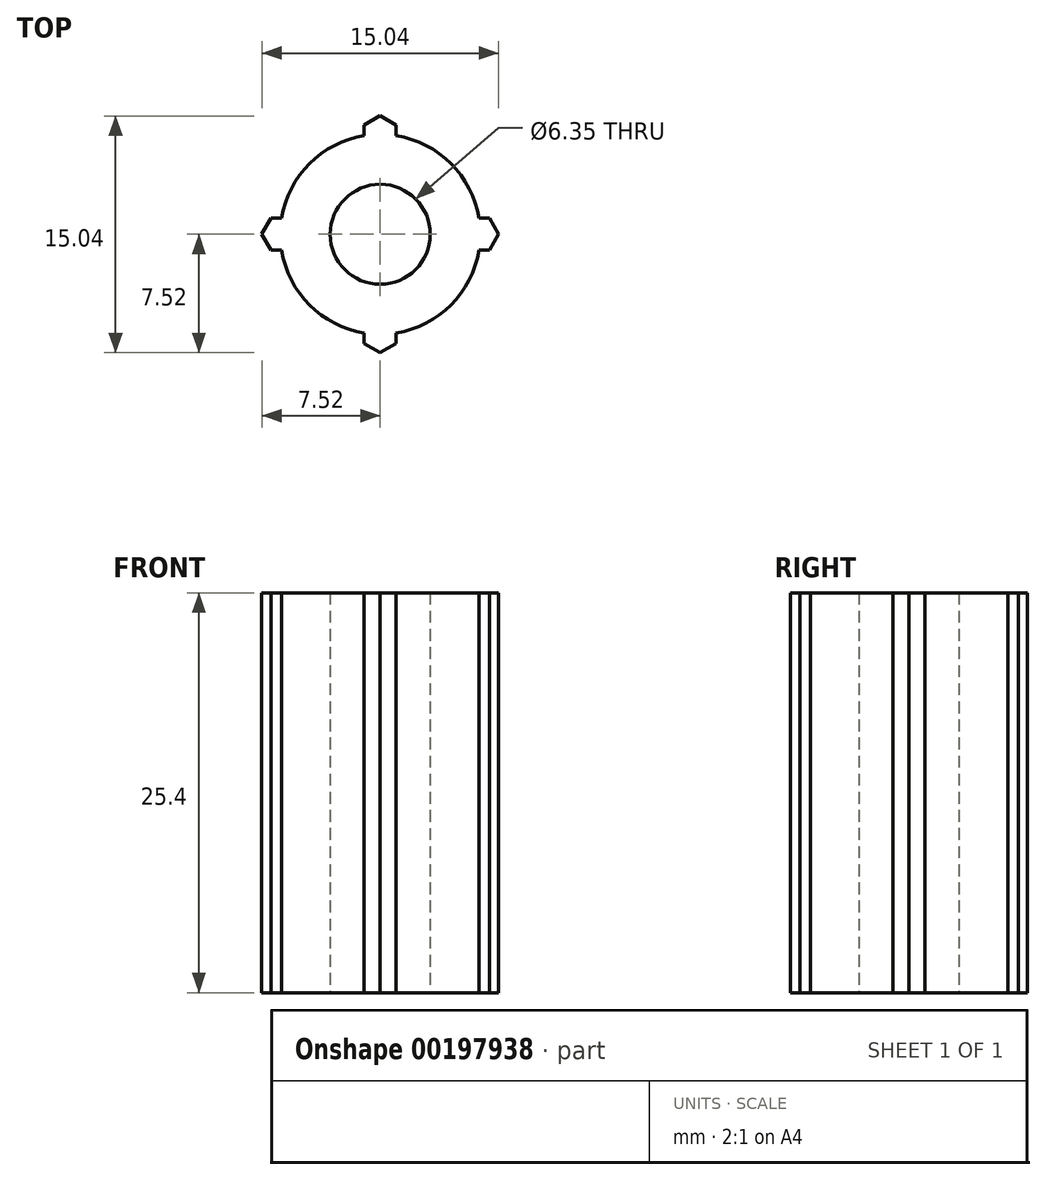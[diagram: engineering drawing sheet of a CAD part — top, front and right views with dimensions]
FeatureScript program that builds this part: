
annotation { "Feature Type Name" : "Feature", "Feature Type Description" : "" }
export const myFeature = defineFeature(function(context is Context, id is Id, definition is map)
    precondition{}
    {
        {
            var Q0;
            Q0=qCreatedBy(makeId("Top.planeOp"),FACE);
            var sketch = newSketch(context, id + "F0", { "sketchPlane" : qUnion([Q0])});
            skCircle(sketch, "E0", {"center": v(0, 0) * mm, "radius": 6.35 * mm});
            skCircle(sketch, "E1.cCircle", {"center": v(-6.35, 0) * mm, "radius": 1.02 * mm, "construction": true});
            skLineSegment(sketch, "E1.0", {"start": v(-6.94, -1.02) * mm, "end": v(-7.52, 0) * mm});
            skLineSegment(sketch, "E1.1", {"start": v(-7.52, 0) * mm, "end": v(-6.94, 1.02) * mm});
            skLineSegment(sketch, "E1.2", {"start": v(-6.94, 1.02) * mm, "end": v(-5.76, 1.02) * mm});
            skLineSegment(sketch, "E1.3", {"start": v(-5.76, 1.02) * mm, "end": v(-5.18, 0) * mm});
            skLineSegment(sketch, "E1.4", {"start": v(-5.18, 0) * mm, "end": v(-5.76, -1.02) * mm});
            skLineSegment(sketch, "E1.5", {"start": v(-5.76, -1.02) * mm, "end": v(-6.94, -1.02) * mm});
            skPoint(sketch, "E1.0.midPoint", {"position": v(-7.23, -0.5) * mm});
            skCircle(sketch, "E2.cCircle", {"center": v(0, 6.35) * mm, "radius": 1.02 * mm, "construction": true});
            skLineSegment(sketch, "E2.0", {"start": v(0, 5.18) * mm, "end": v(-1.02, 5.76) * mm});
            skLineSegment(sketch, "E2.1", {"start": v(-1.02, 5.76) * mm, "end": v(-1.02, 6.94) * mm});
            skLineSegment(sketch, "E2.2", {"start": v(-1.02, 6.94) * mm, "end": v(0, 7.52) * mm});
            skLineSegment(sketch, "E2.3", {"start": v(0, 7.52) * mm, "end": v(1.02, 6.94) * mm});
            skLineSegment(sketch, "E2.4", {"start": v(1.02, 6.94) * mm, "end": v(1.02, 5.76) * mm});
            skLineSegment(sketch, "E2.5", {"start": v(1.02, 5.76) * mm, "end": v(0, 5.18) * mm});
            skPoint(sketch, "E2.0.midPoint", {"position": v(-0.5, 5.47) * mm});
            skCircle(sketch, "E3.cCircle", {"center": v(6.35, 0) * mm, "radius": 1.02 * mm, "construction": true});
            skLineSegment(sketch, "E3.0", {"start": v(7.52, 0) * mm, "end": v(6.94, -1.02) * mm});
            skLineSegment(sketch, "E3.1", {"start": v(6.94, -1.02) * mm, "end": v(5.76, -1.02) * mm});
            skLineSegment(sketch, "E3.2", {"start": v(5.76, -1.02) * mm, "end": v(5.18, 0) * mm});
            skLineSegment(sketch, "E3.3", {"start": v(5.18, 0) * mm, "end": v(5.76, 1.02) * mm});
            skLineSegment(sketch, "E3.4", {"start": v(5.76, 1.02) * mm, "end": v(6.94, 1.02) * mm});
            skLineSegment(sketch, "E3.5", {"start": v(6.94, 1.02) * mm, "end": v(7.52, 0) * mm});
            skPoint(sketch, "E3.0.midPoint", {"position": v(7.23, -0.5) * mm});
            skCircle(sketch, "E4.cCircle", {"center": v(0, -6.35) * mm, "radius": 1.02 * mm, "construction": true});
            skLineSegment(sketch, "E4.0", {"start": v(0, -7.52) * mm, "end": v(-1.02, -6.94) * mm});
            skLineSegment(sketch, "E4.1", {"start": v(-1.02, -6.94) * mm, "end": v(-1.02, -5.76) * mm});
            skLineSegment(sketch, "E4.2", {"start": v(-1.02, -5.76) * mm, "end": v(0, -5.18) * mm});
            skLineSegment(sketch, "E4.3", {"start": v(0, -5.18) * mm, "end": v(1.02, -5.76) * mm});
            skLineSegment(sketch, "E4.4", {"start": v(1.02, -5.76) * mm, "end": v(1.02, -6.94) * mm});
            skLineSegment(sketch, "E4.5", {"start": v(1.02, -6.94) * mm, "end": v(0, -7.52) * mm});
            skPoint(sketch, "E4.0.midPoint", {"position": v(-0.5, -7.23) * mm});
            skCircle(sketch, "E5", {"center": v(0, 0) * mm, "radius": 3.18 * mm});
            skSolve(sketch);
        }
        {
            var Q0;
            Q0 = qSketchRegion(id + "F0", true);
            extrude(context, id + "F1", {"entities" : qUnion([Q0]), "depth" : 25.4 * mm});
        }
    });
